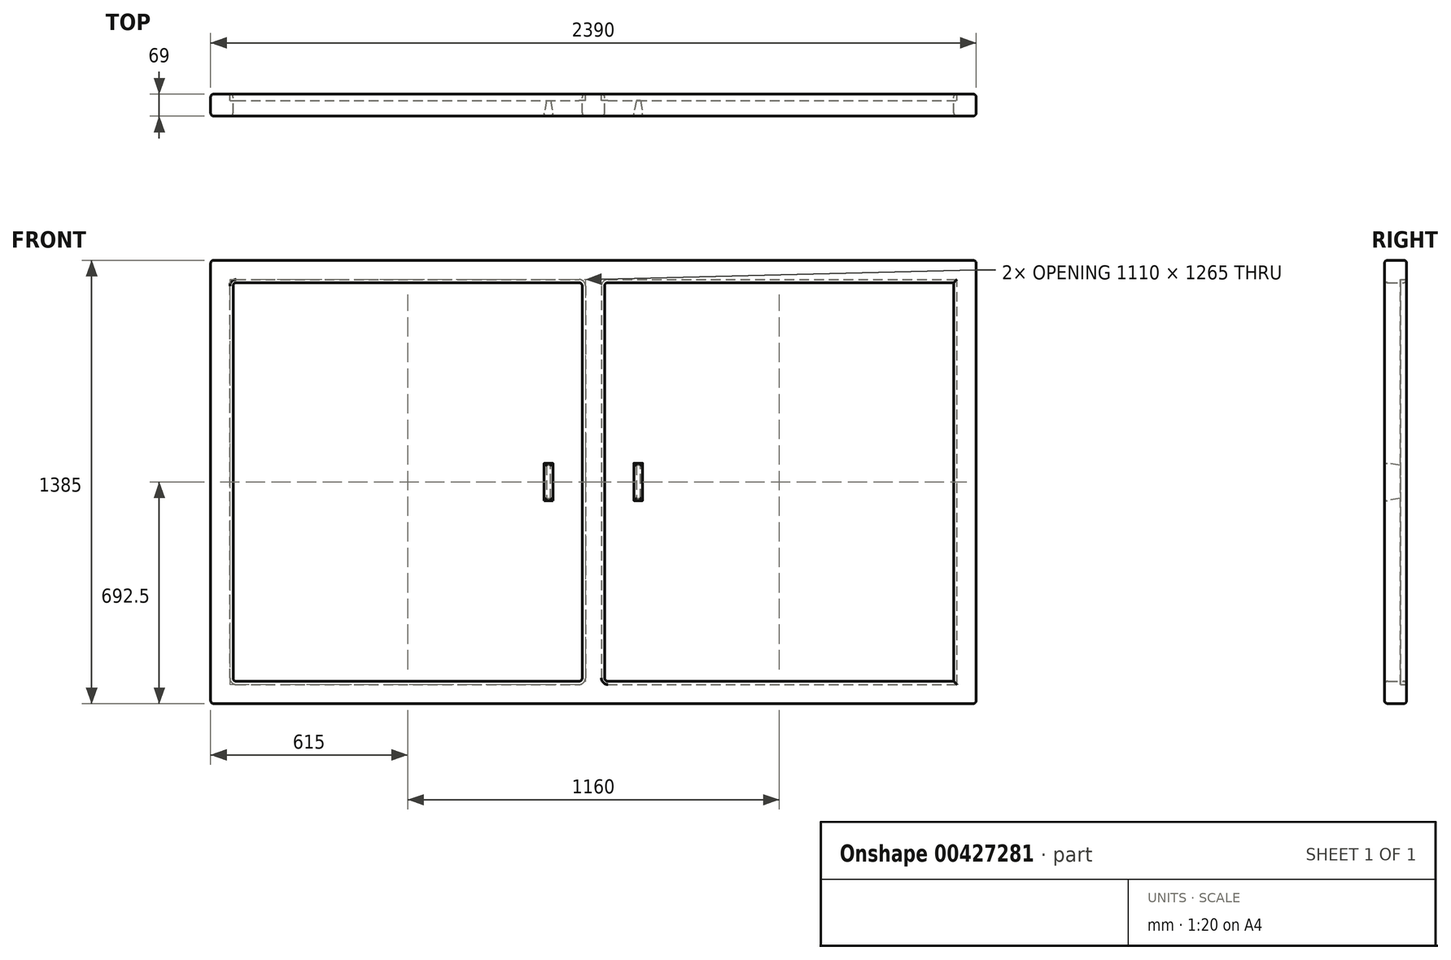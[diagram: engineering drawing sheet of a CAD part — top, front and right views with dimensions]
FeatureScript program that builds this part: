
annotation { "Feature Type Name" : "Feature", "Feature Type Description" : "" }
export const myFeature = defineFeature(function(context is Context, id is Id, definition is map)
    precondition{}
    {
        {
            var Q0;
            Q0=qCreatedBy(makeId("Front.planeOp"),FACE);
            var sketch = newSketch(context, id + "F0", { "sketchPlane" : qUnion([Q0])});
            skLineSegment(sketch, "E0.bottom", {"start": v(0, 0) * mm, "end": v(2390, 0) * mm});
            skLineSegment(sketch, "E0.top", {"start": v(0, 1385) * mm, "end": v(2390, 1385) * mm});
            skLineSegment(sketch, "E0.left", {"start": v(0, 0) * mm, "end": v(0, 1385) * mm});
            skLineSegment(sketch, "E0.right", {"start": v(2390, 0) * mm, "end": v(2390, 1385) * mm});
            skLineSegment(sketch, "E1.0", {"start": v(70, 1315) * mm, "end": v(1160, 1315) * mm});
            skLineSegment(sketch, "E1.1", {"start": v(70, 70) * mm, "end": v(70, 1315) * mm});
            skLineSegment(sketch, "E1.2", {"start": v(70, 70) * mm, "end": v(1160, 70) * mm});
            skLineSegment(sketch, "E1.3", {"start": v(2320, 70) * mm, "end": v(2320, 1315) * mm});
            skLineSegment(sketch, "E2.0", {"start": v(1160, 1315) * mm, "end": v(1160, 70) * mm});
            skLineSegment(sketch, "E3.0", {"start": v(1230, 1315) * mm, "end": v(1230, 70) * mm});
            skPoint(sketch, "E4.end.orphan", {"position": v(1195, 70) * mm});
            skPoint(sketch, "E4.start.orphan", {"position": v(1195, 1315) * mm});
            skLineSegment(sketch, "E5.trimOffspring", {"start": v(1230, 1315) * mm, "end": v(2320, 1315) * mm});
            skLineSegment(sketch, "E6.trimOffspring", {"start": v(1230, 70) * mm, "end": v(2320, 70) * mm});
            skSolve(sketch);
        }
        {
            var Q0;
            Q0=makeQuery(id+"F0.imprint","IMPRINT",FACE,{"disambiguationData":[TD([[makeQuery(id+"F0.imprint","IMPRINT",EDGE,{"derivedFrom":sQuery(id+"F0.wireOp",EDGE,"E0.bottom")}),1.0]])]});
            extrude(context, id + "F1", {"entities" : qUnion([Q0]), "depth" : 69 * mm});
        }
        {
            var Q0;
            Q0=makeQuery(id+"F1.opExtrude","CAP_FACE",FACE,{"disambiguationData":[OSD([sQuery(id+"F0.wireOp",EDGE,"E0.bottom"),sQuery(id+"F0.wireOp",EDGE,"E0.top"),sQuery(id+"F0.wireOp",EDGE,"E0.left"),sQuery(id+"F0.wireOp",EDGE,"E0.right"),sQuery(id+"F0.wireOp",EDGE,"E1.0"),sQuery(id+"F0.wireOp",EDGE,"E1.1"),sQuery(id+"F0.wireOp",EDGE,"E1.2"),sQuery(id+"F0.wireOp",EDGE,"E1.3"),sQuery(id+"F0.wireOp",EDGE,"E2.0"),sQuery(id+"F0.wireOp",EDGE,"E3.0"),sQuery(id+"F0.wireOp",EDGE,"E5.trimOffspring"),sQuery(id+"F0.wireOp",EDGE,"E6.trimOffspring")])],"isStart":false});
            var Q1;
            Q1=makeQuery(id+"F1.opExtrude","CAP_FACE",FACE,{"disambiguationData":[OSD([sQuery(id+"F0.wireOp",EDGE,"E0.bottom"),sQuery(id+"F0.wireOp",EDGE,"E0.top"),sQuery(id+"F0.wireOp",EDGE,"E0.left"),sQuery(id+"F0.wireOp",EDGE,"E0.right"),sQuery(id+"F0.wireOp",EDGE,"E1.0"),sQuery(id+"F0.wireOp",EDGE,"E1.1"),sQuery(id+"F0.wireOp",EDGE,"E1.2"),sQuery(id+"F0.wireOp",EDGE,"E1.3"),sQuery(id+"F0.wireOp",EDGE,"E2.0"),sQuery(id+"F0.wireOp",EDGE,"E3.0"),sQuery(id+"F0.wireOp",EDGE,"E5.trimOffspring"),sQuery(id+"F0.wireOp",EDGE,"E6.trimOffspring")])],"isStart":true});
            var Q2;
            Q2=makeQuery(id+"F1.opExtrude","SWEPT_FACE",FACE,{"disambiguationData":[OSD([sQuery(id+"F0.wireOp",EDGE,"E0.top")])]});
            var Q3;
            Q3=makeQuery(id+"F1.opExtrude","SWEPT_FACE",FACE,{"disambiguationData":[OSD([sQuery(id+"F0.wireOp",EDGE,"E0.right")])]});
            var Q4;
            Q4=makeQuery(id+"F1.opExtrude","SWEPT_FACE",FACE,{"disambiguationData":[OSD([sQuery(id+"F0.wireOp",EDGE,"E1.2")])]});
            var Q5;
            Q5=makeQuery(id+"F1.opExtrude","SWEPT_FACE",FACE,{"disambiguationData":[OSD([sQuery(id+"F0.wireOp",EDGE,"E3.0")])]});
            var Q6;
            Q6=makeQuery(id+"F1.opExtrude","SWEPT_FACE",FACE,{"disambiguationData":[OSD([sQuery(id+"F0.wireOp",EDGE,"E0.bottom")])]});
            var Q7;
            Q7=makeQuery(id+"F1.opExtrude","SWEPT_EDGE",EDGE,{"disambiguationData":[OSD([sQuery(id+"F0.wireOp",EDGE,"E1.0"),sQuery(id+"F0.wireOp",EDGE,"E2.0")])]});
            var Q8;
            Q8=makeQuery(id+"F1.opExtrude","SWEPT_EDGE",EDGE,{"disambiguationData":[OSD([sQuery(id+"F0.wireOp",EDGE,"E1.0"),sQuery(id+"F0.wireOp",EDGE,"E1.1")])]});
            fillet(context, id + "F2", {"entities" : qUnion([Q0, Q1, Q2, Q3, Q4, Q5, Q6, Q7, Q8]), "radius" : 10 * mm, "tangentPropagation" : true, "allowEdgeOverflow" : false});
        }
        {
            var Q0;
            Q0=qCreatedBy(makeId("Front.planeOp"),FACE);
            var sketch = newSketch(context, id + "F3", { "sketchPlane" : qUnion([Q0])});
            skLineSegment(sketch, "E7.0", {"start": v(1320, 632.5) * mm, "end": v(1320, 752.5) * mm});
            skLineSegment(sketch, "E8", {"start": v(1320, 692.5) * mm, "end": v(1320, 752.5) * mm});
            skLineSegment(sketch, "E9", {"start": v(1320, 752.5) * mm, "end": v(1350, 752.5) * mm});
            skLineSegment(sketch, "E10", {"start": v(1350, 752.5) * mm, "end": v(1350, 632.5) * mm});
            skLineSegment(sketch, "E11", {"start": v(1350, 632.5) * mm, "end": v(1320, 632.5) * mm});
            skLineSegment(sketch, "E12.0", {"start": v(5, 5) * mm, "end": v(2385, 5) * mm});
            skLineSegment(sketch, "E12.1", {"start": v(5, 1380) * mm, "end": v(5, 5) * mm});
            skLineSegment(sketch, "E12.2", {"start": v(2385, 1380) * mm, "end": v(5, 1380) * mm});
            skLineSegment(sketch, "E12.3", {"start": v(2385, 5) * mm, "end": v(2385, 1380) * mm});
            skLineSegment(sketch, "E13.0", {"start": v(1195, 1305) * mm, "end": v(1195, 80) * mm});
            skPoint(sketch, "E14.orphan", {"position": v(1320, 1305) * mm});
            skPoint(sketch, "E15.orphan", {"position": v(1320, 80) * mm});
            skLineSegment(sketch, "E16.MirrorCS", {"start": v(1070, 692.5) * mm, "end": v(1070, 752.5) * mm});
            skLineSegment(sketch, "E17.MirrorCS", {"start": v(1070, 632.5) * mm, "end": v(1070, 752.5) * mm});
            skLineSegment(sketch, "E18.MirrorCS", {"start": v(1040, 632.5) * mm, "end": v(1070, 632.5) * mm});
            skLineSegment(sketch, "E19.MirrorCS", {"start": v(1040, 752.5) * mm, "end": v(1040, 632.5) * mm});
            skLineSegment(sketch, "E20.MirrorCS", {"start": v(1070, 752.5) * mm, "end": v(1040, 752.5) * mm});
            skSolve(sketch);
        }
        {
            var Q0;
            Q0=makeQuery(id+"F1.opExtrude","CAP_FACE",FACE,{"disambiguationData":[OSD([sQuery(id+"F0.wireOp",EDGE,"E0.bottom"),sQuery(id+"F0.wireOp",EDGE,"E0.top"),sQuery(id+"F0.wireOp",EDGE,"E0.left"),sQuery(id+"F0.wireOp",EDGE,"E0.right"),sQuery(id+"F0.wireOp",EDGE,"E1.0"),sQuery(id+"F0.wireOp",EDGE,"E1.1"),sQuery(id+"F0.wireOp",EDGE,"E1.2"),sQuery(id+"F0.wireOp",EDGE,"E1.3"),sQuery(id+"F0.wireOp",EDGE,"E2.0"),sQuery(id+"F0.wireOp",EDGE,"E3.0"),sQuery(id+"F0.wireOp",EDGE,"E5.trimOffspring"),sQuery(id+"F0.wireOp",EDGE,"E6.trimOffspring")])],"isStart":true});
            var sketch = newSketch(context, id + "F4", { "sketchPlane" : qUnion([Q0])});
            skLineSegment(sketch, "E21.0", {"start": v(-2330, 60) * mm, "end": v(-2330, 1325) * mm});
            skArc(sketch, "E21.1", {"start": v(-1220, 1305) * mm, "mid": v(-1225.86, 1319.14) * mm, "end": v(-1240, 1325) * mm});
            skLineSegment(sketch, "E21.2", {"start": v(-1220, 1305) * mm, "end": v(-1220, 80) * mm});
            skLineSegment(sketch, "E21.3", {"start": v(-2330, 1325) * mm, "end": v(-1240, 1325) * mm});
            skArc(sketch, "E21.4", {"start": v(-1240, 60) * mm, "mid": v(-1225.86, 65.86) * mm, "end": v(-1220, 80) * mm});
            skLineSegment(sketch, "E21.5", {"start": v(-1240, 60) * mm, "end": v(-2330, 60) * mm});
            skArc(sketch, "E22.0", {"start": v(-1150, 1325) * mm, "mid": v(-1164.14, 1319.14) * mm, "end": v(-1170, 1305) * mm});
            skLineSegment(sketch, "E22.1", {"start": v(-1170, 80) * mm, "end": v(-1170, 1305) * mm});
            skLineSegment(sketch, "E22.2", {"start": v(-1150, 1325) * mm, "end": v(-80, 1325) * mm});
            skArc(sketch, "E22.3", {"start": v(-1170, 80) * mm, "mid": v(-1164.14, 65.86) * mm, "end": v(-1150, 60) * mm});
            skArc(sketch, "E22.4", {"start": v(-60, 1305) * mm, "mid": v(-65.86, 1319.14) * mm, "end": v(-80, 1325) * mm});
            skLineSegment(sketch, "E22.5", {"start": v(-60, 1305) * mm, "end": v(-60, 80) * mm});
            skArc(sketch, "E22.6", {"start": v(-80, 60) * mm, "mid": v(-65.86, 65.86) * mm, "end": v(-60, 80) * mm});
            skLineSegment(sketch, "E22.7", {"start": v(-80, 60) * mm, "end": v(-1150, 60) * mm});
            skSolve(sketch);
        }
        {
            var Q0;
            Q0=qSketchRegion(id+"F4",true);
            extrude(context, id + "F5", {"entities" : qUnion([Q0]), "oppositeDirection" : true, "depth" : 20 * mm});
        }
        {
            var Q0;
            Q0=makeQuery(id+"F1.opExtrude","CAP_FACE",FACE,{"disambiguationData":[OSD([sQuery(id+"F0.wireOp",EDGE,"E0.bottom"),sQuery(id+"F0.wireOp",EDGE,"E0.top"),sQuery(id+"F0.wireOp",EDGE,"E0.left"),sQuery(id+"F0.wireOp",EDGE,"E0.right"),sQuery(id+"F0.wireOp",EDGE,"E1.0"),sQuery(id+"F0.wireOp",EDGE,"E1.1"),sQuery(id+"F0.wireOp",EDGE,"E1.2"),sQuery(id+"F0.wireOp",EDGE,"E1.3"),sQuery(id+"F0.wireOp",EDGE,"E2.0"),sQuery(id+"F0.wireOp",EDGE,"E3.0"),sQuery(id+"F0.wireOp",EDGE,"E5.trimOffspring"),sQuery(id+"F0.wireOp",EDGE,"E6.trimOffspring")])],"isStart":false});
            var sketch = newSketch(context, id + "F6", { "sketchPlane" : qUnion([Q0])});
            skLineSegment(sketch, "E23.0", {"start": v(1350, 632.5) * mm, "end": v(1350, 752.5) * mm});
            skLineSegment(sketch, "E23.1", {"start": v(1320, 632.5) * mm, "end": v(1350, 632.5) * mm});
            skLineSegment(sketch, "E23.2", {"start": v(1350, 752.5) * mm, "end": v(1320, 752.5) * mm});
            skLineSegment(sketch, "E23.3", {"start": v(1320, 752.5) * mm, "end": v(1320, 692.5) * mm});
            skLineSegment(sketch, "E23.4", {"start": v(1320, 692.5) * mm, "end": v(1320, 632.5) * mm});
            skLineSegment(sketch, "E24.0", {"start": v(1070, 752.5) * mm, "end": v(1040, 752.5) * mm});
            skLineSegment(sketch, "E24.1", {"start": v(1070, 692.5) * mm, "end": v(1070, 752.5) * mm});
            skLineSegment(sketch, "E24.2", {"start": v(1040, 752.5) * mm, "end": v(1040, 632.5) * mm});
            skLineSegment(sketch, "E24.3", {"start": v(1040, 632.5) * mm, "end": v(1070, 632.5) * mm});
            skLineSegment(sketch, "E24.4", {"start": v(1070, 632.5) * mm, "end": v(1070, 692.5) * mm});
            skSolve(sketch);
        }
        {
            var Q0;
            Q0=makeQuery(id+"F6.imprint","IMPRINT",FACE,{"disambiguationData":[TD([[makeQuery(id+"F6.imprint","IMPRINT",EDGE,{"derivedFrom":sQuery(id+"F6.wireOp",EDGE,"E24.0")}),1.0]])]});
            var Q1;
            Q1=makeQuery(id+"F6.imprint","IMPRINT",FACE,{"disambiguationData":[TD([[makeQuery(id+"F6.imprint","IMPRINT",EDGE,{"derivedFrom":sQuery(id+"F6.wireOp",EDGE,"E23.0")}),1.0]])]});
            extrude(context, id + "F7", {"entities" : qUnion([Q0, Q1]), "endBound" : BoundingType.UP_TO_NEXT, "oppositeDirection" : true, "depth" : 25 * mm, "hasDraft" : true, "draftAngle" : 10 * degree, "draftPullDirection" : true});
        }
        {
            var Q0;
            Q0=makeQuery(id+"F7.opExtrude","CAP_FACE",FACE,{"disambiguationData":[OSD([sQuery(id+"F6.wireOp",EDGE,"E23.0"),sQuery(id+"F6.wireOp",EDGE,"E23.1"),sQuery(id+"F6.wireOp",EDGE,"E23.2"),sQuery(id+"F6.wireOp",EDGE,"E23.3"),sQuery(id+"F6.wireOp",EDGE,"E23.4")])],"isStart":true});
            var Q1;
            Q1=makeQuery(id+"F7.opExtrude","CAP_FACE",FACE,{"disambiguationData":[OSD([sQuery(id+"F6.wireOp",EDGE,"E24.0"),sQuery(id+"F6.wireOp",EDGE,"E24.1"),sQuery(id+"F6.wireOp",EDGE,"E24.2"),sQuery(id+"F6.wireOp",EDGE,"E24.3"),sQuery(id+"F6.wireOp",EDGE,"E24.4")])],"isStart":true});
            fillet(context, id + "F8", {"entities" : qUnion([Q0, Q1]), "radius" : 7.5 * mm, "tangentPropagation" : true, "allowEdgeOverflow" : false});
        }
    });
